# Revit family: Electronics_Visual-TVs_ViewSonic_The-ViewSonicR-CDE8600-Series-Large-Form
name_source: partatom
category: Electrical Equipment
revit_build: Autodesk Revit 2015 (Build: 20140606_1530(x64)
units: mm (PartAtom-declared; Revit-internal decimal feet)

## types (1)
- CDE8600
    Assembly Code = D50
    BIMobject category = Visual - TVs
    BIMobject category code = electronics-visual-tvs
    BIMobject main category = Electronics
    BIMobject main category code = electronics
    BOSUseNativeGeometries = 1
    Brand url = https://www.viewsonic.com
    Covering Color = Plastic - Viewsonic - Black
    Description = The ViewSonic® CDE8600 is an 86" (85.6’’viewable) 4K Ultra HD commercial display that delivers high reliability at a great value, 16 hours a day, 7 days a week. An embedded Android SOC allows you to install Android apps for rich content broadcasting, while a convenient built-in browser displays internet content without the need for a PC. Bundled ViewBoard® Cast™ software enables content streaming from mobile devices onto the display over wireless or cable networks. In addition to HDMI, DisplayPort, VGA, USB, IR, and RJ45 inputs, this display utilizes an integrated multi-core processor and 16GB of internal memory, allowing customers to playback multimedia content via USB without the need for a PC. With stunning 3840x2160 resolution, 350-nit high brightness, wide viewing angles, and dual 20W speakers, this display provides immersive, high-impact messaging wherever needed. To make life even easier, the bundled vController software offers easy maintenance and intuitive interfaces for remote management via a PC server or laptop, and its flicker-free and blue light filter technologies help provide a comfortable viewing environment.
    Design country = Taiwan
    Edition number = 1
    Installation instructions = http://www.viewsonicglobal.com
    Keynote = V90
    Manufacturer = ViewSonic
    Manufacturer country = Taiwan
    Manufacturer name = ViewSonic
    Model = viewsonic_cde8600
    Product Guid = 1ff7a197-bb83-4c15-bf79-ff5a29525ea3
    Product SKU = viewsonic_cde8600
    Product data url = https://bimobject.com
    Product family = Electronics
    Product group = Large Format Displays
    Product name = The ViewSonic® CDE8600 Series Large Format Displays
    Product url = https://www.viewsonic.com
    QR code = http://bimobject.com
    Technical description = http://www.viewsonicglobal.com
    URL = www.viewsonic.com
    Youtube clip = https://www.youtube.com

## geometry (parser evidence)
native form markers: Sweep x3
no freeform markers — native parametric forms only
